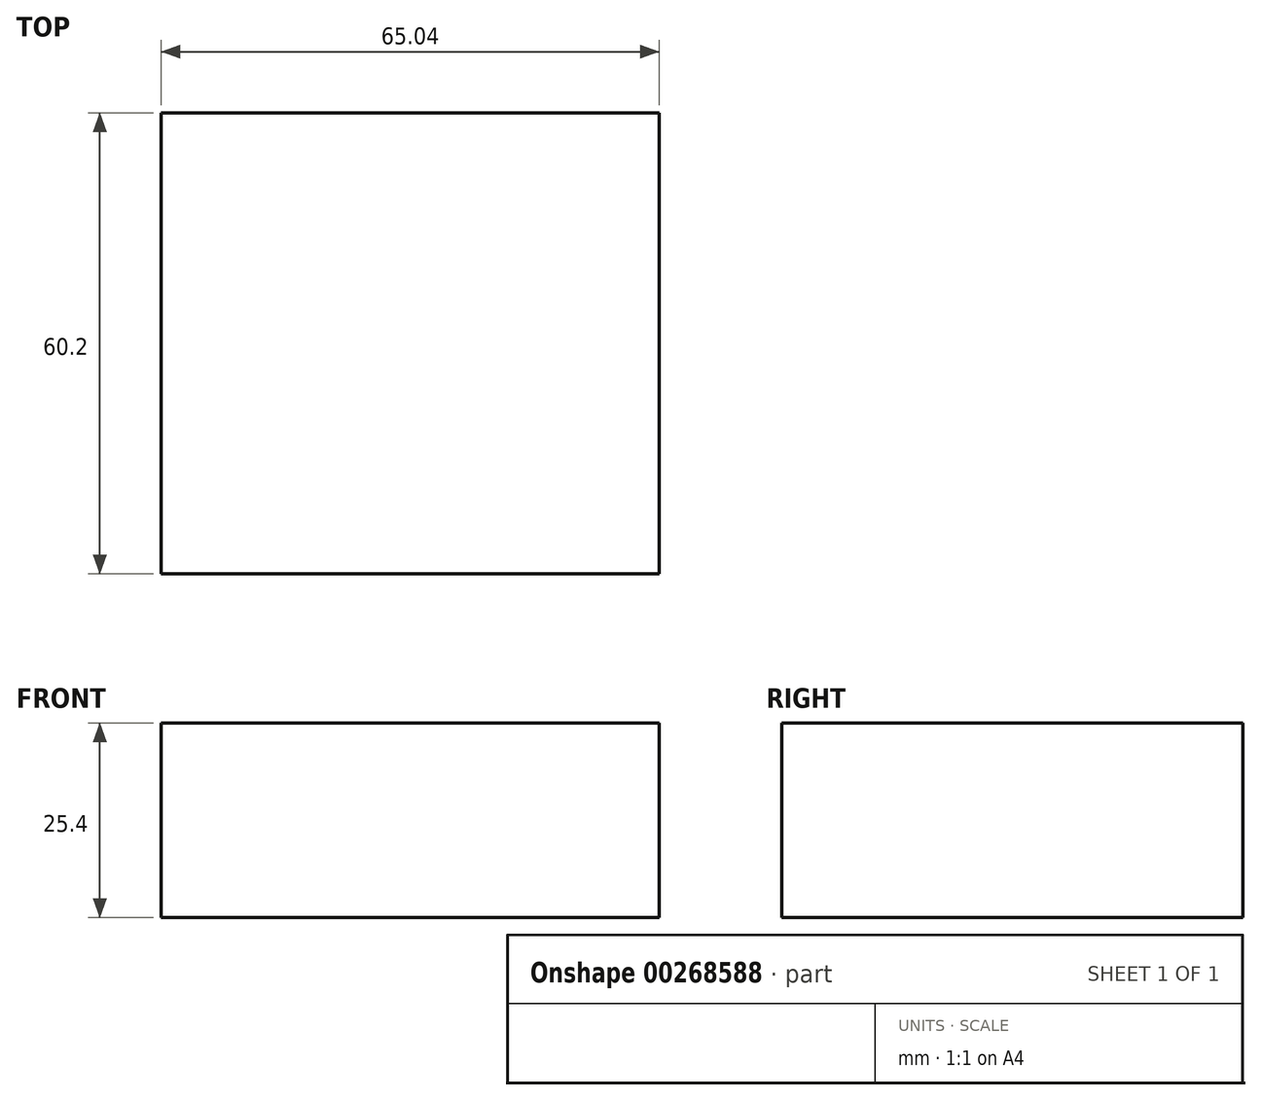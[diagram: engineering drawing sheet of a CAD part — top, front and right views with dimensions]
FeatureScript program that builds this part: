
annotation { "Feature Type Name" : "Feature", "Feature Type Description" : "" }
export const myFeature = defineFeature(function(context is Context, id is Id, definition is map)
    precondition{}
    {
        {
            var Q0;
            Q0=qCreatedBy(makeId("Top.planeOp"),FACE);
            var sketch = newSketch(context, id + "F0", { "sketchPlane" : qUnion([Q0])});
            skLineSegment(sketch, "E0.bottom", {"start": v(-32.52, 30.1) * mm, "end": v(32.52, 30.1) * mm});
            skLineSegment(sketch, "E0.top", {"start": v(-32.52, -30.1) * mm, "end": v(32.52, -30.1) * mm});
            skLineSegment(sketch, "E0.left", {"start": v(-32.52, 30.1) * mm, "end": v(-32.52, -30.1) * mm});
            skLineSegment(sketch, "E0.right", {"start": v(32.52, 30.1) * mm, "end": v(32.52, -30.1) * mm});
            skPoint(sketch, "E0.middle", {"position": v(0, 0) * mm});
            skSolve(sketch);
        }
        {
            var Q0;
            Q0 = qSketchRegion(id + "F0", true);
            extrude(context, id + "F1", {"entities" : qUnion([Q0]), "depth" : 25.4 * mm});
        }
    });
